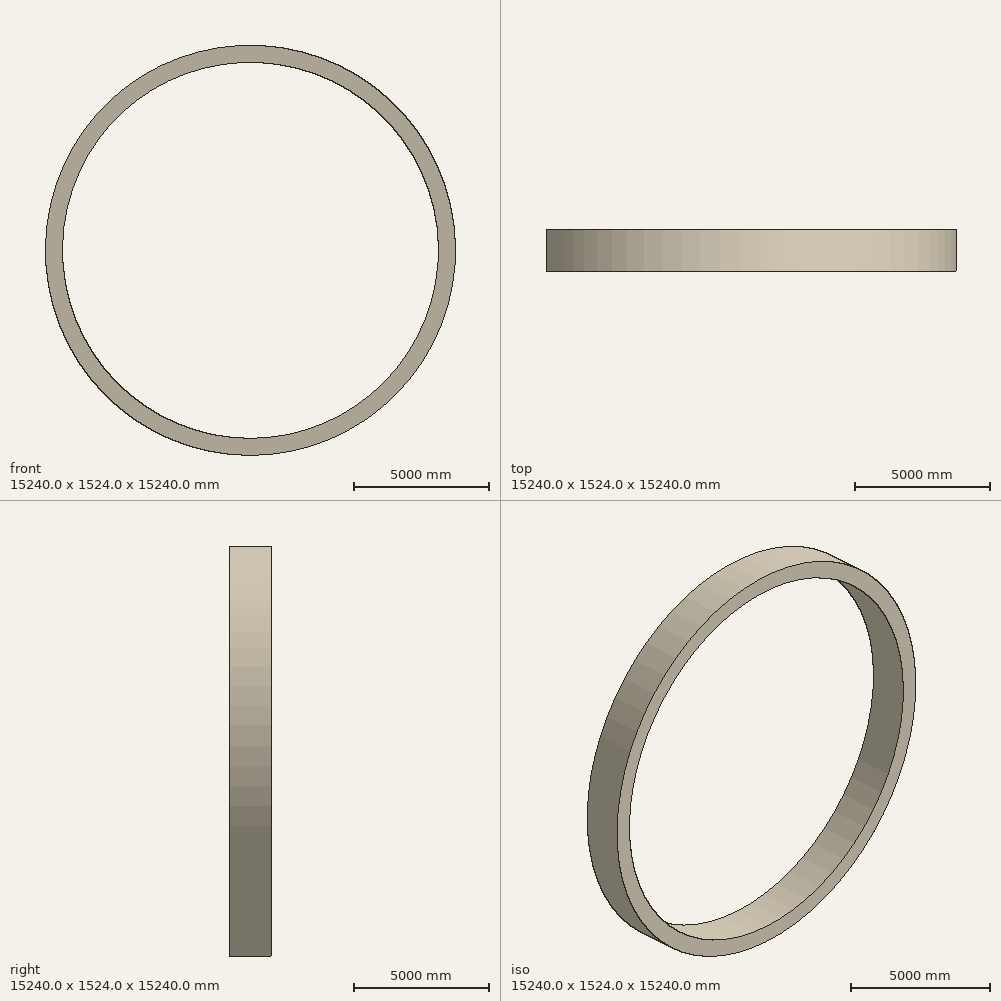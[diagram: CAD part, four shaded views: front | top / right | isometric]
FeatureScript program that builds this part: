
annotation { "Feature Type Name" : "Feature", "Feature Type Description" : "" }
export const myFeature = defineFeature(function(context is Context, id is Id, definition is map)
    precondition{}
    {
        {
            var Q0;
            Q0=qCreatedBy(makeId("Front.planeOp"),FACE);
            var sketch = newSketch(context, id + "F0", { "sketchPlane" : qUnion([Q0])});
            skCircle(sketch, "E0", {"center": v(0, 0) * mm, "radius": 7620 * mm});
            skSolve(sketch);
        }
        {
            var Q0;
            Q0=makeQuery(id+"F0.imprint","IMPRINT",FACE,{"disambiguationData":[TD([[makeQuery(id+"F0.imprint","IMPRINT",EDGE,{"derivedFrom":sQuery(id+"F0.wireOp",EDGE,"E0")}),1.0]])]});
            var sketch = newSketch(context, id + "F1", { "sketchPlane" : qUnion([Q0])});
            skCircle(sketch, "E1", {"center": v(0, 0) * mm, "radius": 6985 * mm});
            skSolve(sketch);
        }
        {
            var Q0;
            Q0 = qSketchRegion(id + "F0", true);
            extrude(context, id + "F2", {"entities" : qUnion([Q0]), "depth" : 1524 * mm});
        }
        {
            var Q0;
            Q0 = qSketchRegion(id + "F1", true);
            extrude(context, id + "F3", {"entities" : qUnion([Q0]), "operationType" : NewBodyOperationType.REMOVE, "depth" : 7874 * mm});
        }
    });
